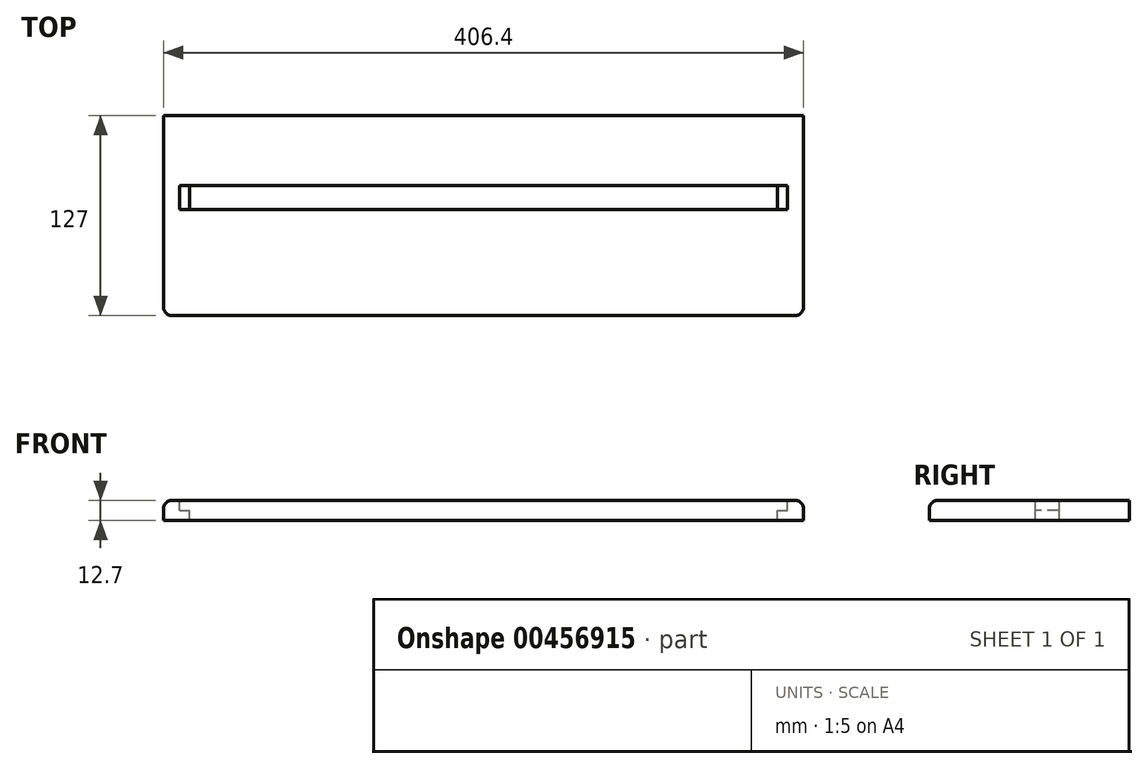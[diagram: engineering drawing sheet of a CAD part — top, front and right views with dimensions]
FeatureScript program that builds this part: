
annotation { "Feature Type Name" : "Feature", "Feature Type Description" : "" }
export const myFeature = defineFeature(function(context is Context, id is Id, definition is map)
    precondition{}
    {
        {
            var Q0;
            Q0=qCreatedBy(makeId("Top.planeOp"),FACE);
            var sketch = newSketch(context, id + "F0", { "sketchPlane" : qUnion([Q0])});
            skLineSegment(sketch, "E0.bottom", {"start": v(-406.4, 127) * mm, "end": v(0, 127) * mm});
            skLineSegment(sketch, "E0.top", {"start": v(-406.4, 0) * mm, "end": v(0, 0) * mm});
            skLineSegment(sketch, "E0.left", {"start": v(-406.4, 127) * mm, "end": v(-406.4, 0) * mm});
            skLineSegment(sketch, "E0.right", {"start": v(0, 127) * mm, "end": v(0, 0) * mm});
            skSolve(sketch);
        }
        {
            var Q0;
            Q0=makeQuery(id+"F0.imprint","IMPRINT",FACE,{"disambiguationData":[TD([[makeQuery(id+"F0.imprint","IMPRINT",EDGE,{"derivedFrom":sQuery(id+"F0.wireOp",EDGE,"E0.bottom")}),-1.0]])]});
            extrude(context, id + "F1", {"entities" : qUnion([Q0]), "depth" : 12.7 * mm});
        }
        {
            var Q0;
            Q0=makeQuery(id+"F1.opExtrude","CAP_EDGE",EDGE,{"disambiguationData":[OSD([sQuery(id+"F0.wireOp",EDGE,"E0.top")])],"isStart":false});
            fillet(context, id + "F2", {"entities" : qUnion([Q0]), "radius" : 5.08 * mm, "tangentPropagation" : true, "allowEdgeOverflow" : false});
        }
        {
            var Q0;
            Q0=makeQuery(id+"F1.opExtrude","CAP_EDGE",EDGE,{"disambiguationData":[OSD([sQuery(id+"F0.wireOp",EDGE,"E0.left")])],"isStart":false});
            var Q1;
            Q1=makeQuery(id+"F1.opExtrude","CAP_EDGE",EDGE,{"disambiguationData":[OSD([sQuery(id+"F0.wireOp",EDGE,"E0.right")])],"isStart":false});
            fillet(context, id + "F3", {"entities" : qUnion([Q0, Q1]), "radius" : 5.08 * mm, "tangentPropagation" : true, "allowEdgeOverflow" : false});
        }
        {
            var Q0;
            Q0=makeQuery(id+"F1.opExtrude","CAP_FACE",FACE,{"disambiguationData":[OSD([sQuery(id+"F0.wireOp",EDGE,"E0.bottom"),sQuery(id+"F0.wireOp",EDGE,"E0.top"),sQuery(id+"F0.wireOp",EDGE,"E0.left"),sQuery(id+"F0.wireOp",EDGE,"E0.right")])],"isStart":false});
            var sketch = newSketch(context, id + "F4", { "sketchPlane" : qUnion([Q0])});
            skLineSegment(sketch, "E1", {"start": v(-396.24, 82.55) * mm, "end": v(-10.16, 82.55) * mm});
            skLineSegment(sketch, "E2", {"start": v(-10.16, 82.55) * mm, "end": v(-10.16, 67.3) * mm});
            skLineSegment(sketch, "E3", {"start": v(-10.16, 67.3) * mm, "end": v(-396.24, 67.3) * mm});
            skLineSegment(sketch, "E4", {"start": v(-396.24, 67.3) * mm, "end": v(-396.24, 82.55) * mm});
            skPoint(sketch, "E5", {"position": v(-203.2, 127) * mm});
            skPoint(sketch, "E6", {"position": v(-203.2, 82.55) * mm});
            skSolve(sketch);
        }
        {
            var Q0;
            Q0=makeQuery(id+"F4.imprint","IMPRINT",FACE,{"disambiguationData":[TD([[makeQuery(id+"F4.imprint","IMPRINT",EDGE,{"derivedFrom":sQuery(id+"F4.wireOp",EDGE,"E1")}),-1.0]])]});
            extrude(context, id + "F5", {"entities" : qUnion([Q0]), "operationType" : NewBodyOperationType.REMOVE, "oppositeDirection" : true, "depth" : 6.35 * mm});
        }
        {
            var Q0;
            Q0=makeQuery(id+"F5.boolean.opBoolean","COPY",FACE,{"derivedFrom":makeQuery(id+"F5.opExtrude","CAP_FACE",FACE,{"disambiguationData":[OSD([sQuery(id+"F4.wireOp",EDGE,"E1"),sQuery(id+"F4.wireOp",EDGE,"E2"),sQuery(id+"F4.wireOp",EDGE,"E3"),sQuery(id+"F4.wireOp",EDGE,"E4")])],"isStart":false})});
            var sketch = newSketch(context, id + "F6", { "sketchPlane" : qUnion([Q0])});
            skPoint(sketch, "E7", {"position": v(-389.9, 82.55) * mm});
            skPoint(sketch, "E8", {"position": v(-389.9, 67.3) * mm});
            skPoint(sketch, "E9", {"position": v(-16.51, 82.55) * mm});
            skPoint(sketch, "E10", {"position": v(-16.51, 67.3) * mm});
            skLineSegment(sketch, "E11", {"start": v(-389.9, 82.55) * mm, "end": v(-389.9, 67.3) * mm});
            skLineSegment(sketch, "E12", {"start": v(-16.51, 67.3) * mm, "end": v(-16.51, 82.55) * mm});
            skLineSegment(sketch, "E13", {"start": v(-16.51, 82.55) * mm, "end": v(-389.9, 82.55) * mm});
            skLineSegment(sketch, "E14", {"start": v(-389.9, 67.3) * mm, "end": v(-16.51, 67.3) * mm});
            skSolve(sketch);
        }
        {
            var Q0;
            Q0=makeQuery(id+"F6.imprint","IMPRINT",FACE,{"disambiguationData":[TD([[makeQuery(id+"F6.imprint","IMPRINT",EDGE,{"derivedFrom":sQuery(id+"F6.wireOp",EDGE,"E11")}),1.0]])]});
            extrude(context, id + "F7", {"entities" : qUnion([Q0]), "operationType" : NewBodyOperationType.REMOVE, "oppositeDirection" : true, "depth" : 6.35 * mm});
        }
    });
